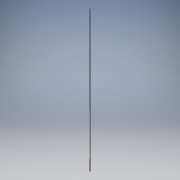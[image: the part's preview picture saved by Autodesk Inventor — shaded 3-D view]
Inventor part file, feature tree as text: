
AUTODESK INVENTOR PART (.ipt)
format: ipt  version: 2016 (Build 200138000, 138)  size: 162,304 bytes
history: native  units: mm
features: other x2, sheet_metal_op x2, sketch x2, chamfer x1, extrude x1, pattern_linear x1
ambient origin geometry x8: Origin, YZ Plane, XZ Plane, XY Plane, X Axis, Y Axis, Z Axis, Center Point
bodies: Solid1 (feature_tree)
feature tree (9):
  parser-record x1  (decoder bookkeeping rows leaked as tree rows — omitted from the tree; the rows remain in map.json)
  sheet_metal_op  "Contour Flange1"
  chamfer  "Corner Round1"
  extrude  "Extrusion1"  Depth=20.0mm
  pattern_linear  "Rectangular Pattern1"  Spacing1=3.0mm  [1 undecoded]
  sketch  "Sketch1"  dims[d0=20.0mm d1=20.0mm]
  other  "Plate1"
  sheet_metal_op  "Bend1"
  sketch  "Sketch2"  dims[d2=44.0mm d3=3.0mm d4=1.5mm d5=6.0mm d6=3.0mm d8=3.0mm d9=3.0mm d10=12.0mm d11=3.0mm d12=3.0mm d13=6.0mm d16=9.525mm d18=9.525mm d19=9.525mm d21=10.0mm d22=0.0mm d23=20.0mm d25=448.6275mm]
note: 1 required parameter value undecoded (feature->parameter linkage not recoverable at this tier; creation-order binding heuristic only, values carry confidence <= 0.55)
note: 1 file-system path scrubbed to <path> (originals preserved in map.json)
